# Revit family: Gira_026230
name_source: partatom
category: Electrical Fixtures
revit_build: Autodesk Revit 2017 (Build: 20160225_1515(x64)
units: mm (PartAtom-declared; Revit-internal decimal feet)

## family parameters
Cut with Voids When Loaded = No
Host = Face
Maintain Annotation Orientation = No
Part Type = Normal
Room Calculation Point = No
Round Connector Dimension = Use Diameter
Shared = No

## types (1)
- Hous. HC + in.sp. ins. comm.tec WP SM grey
    Assembly arrangement = Basic element with complete housing
    BIM = https://media.live.bim.site
    BIMSITE_PRODUCT_ID = a0636f71108af675a756d221536b3fa05e802baf
    Colour = Grey
    Cost = 0 $
    Default Elevation = 1219 mm
    Description = Hous.HC in.sp.ins.comm.tec WP SM GY Housing with hinged cover and inscription space for communication technology inserts,grey Notes : - Not suitable for AMP Communications Outlet (ACO), IBM ACS-System, Reichle de Massari ACS-System, IBM STPA, ST SC Simplex Duplex, Telegärtner OCS-System, IBM ACS Mini-C 600 MHz and WBT high-end speaker connectors.
    GTIN = 4010337262305
    HAN = 026230
    Halogen free = Yes
    HeinzeBIM = https://www.heinze.de
    Imprintable label = With indication plate
    Luster terminal = No
    Manufacturer = Gira
    Material = plastic
    Material quality = Thermoplastic
    Suitable for degree of protection (IP) = IP44
    Support ring = No
    Surface finishing = Not applicable
    Surface protection = Sonstige (*de-DE)
    Transparent = No
    Type of fastening = Mounting with screw
    URL = https://www.gira.de
    Utilization = For data connection housing
    With dust cover = No
    With hinged lid = Yes
    With imprint = No
    With strain relief = No

## geometry (parser evidence)
native form markers: Blend x2, Sweep x6
no freeform markers — native parametric forms only
